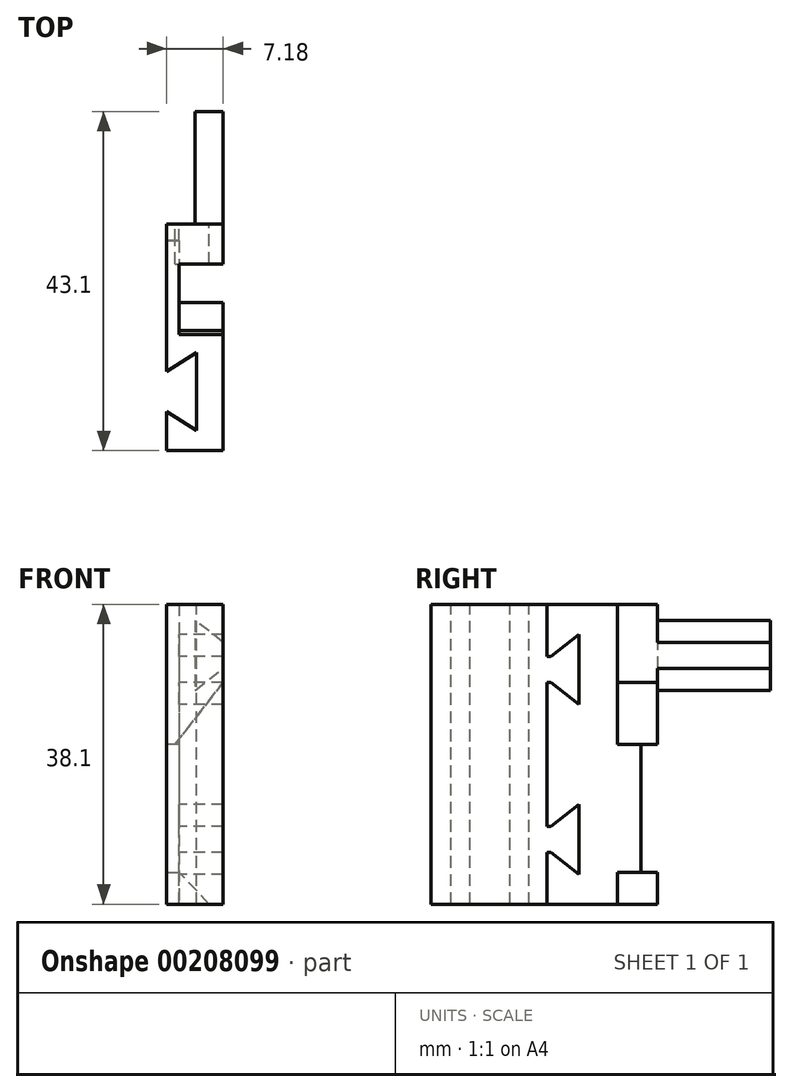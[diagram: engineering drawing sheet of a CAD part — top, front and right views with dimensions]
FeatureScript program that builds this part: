
annotation { "Feature Type Name" : "Feature", "Feature Type Description" : "" }
export const myFeature = defineFeature(function(context is Context, id is Id, definition is map)
    precondition{}
    {
        {
            var Q0;
            Q0=qCreatedBy(makeId("Right.planeOp"),FACE);
            var sketch = newSketch(context, id + "F0", { "sketchPlane" : qUnion([Q0])});
            skLineSegment(sketch, "E0.bottom", {"start": v(-15.24, 38.1) * mm, "end": v(11.43, 38.1) * mm});
            skLineSegment(sketch, "E0.top", {"start": v(-15.24, 0) * mm, "end": v(11.43, 0) * mm});
            skLineSegment(sketch, "E0.right", {"start": v(11.43, 38.1) * mm, "end": v(11.43, 0) * mm});
            skLineSegment(sketch, "E1", {"start": v(-15.24, 38.1) * mm, "end": v(-15.24, 0) * mm});
            skLineSegment(sketch, "E2.bottom", {"start": v(11.43, 38.1) * mm, "end": v(13.54, 38.1) * mm});
            skLineSegment(sketch, "E2.top", {"start": v(11.43, 20.32) * mm, "end": v(13.54, 20.32) * mm});
            skLineSegment(sketch, "E2.left", {"start": v(11.43, 38.1) * mm, "end": v(11.43, 20.32) * mm});
            skLineSegment(sketch, "E2.right", {"start": v(13.54, 38.1) * mm, "end": v(13.54, 20.32) * mm});
            skSolve(sketch);
        }
        {
            var Q0;
            Q0 = qSketchRegion(id + "F0", true);
            extrude(context, id + "F1", {"entities" : qUnion([Q0]), "depth" : 1.59 * mm});
        }
        {
            var Q0;
            Q0=makeQuery(id+"F1.opExtrude","CAP_FACE",FACE,{"disambiguationData":[OSD([sQuery(id+"F0.wireOp",EDGE,"E0.bottom"),sQuery(id+"F0.wireOp",EDGE,"E0.top"),sQuery(id+"F0.wireOp",EDGE,"E0.right"),sQuery(id+"F0.wireOp",EDGE,"E1")])],"isStart":false});
            var sketch = newSketch(context, id + "F2", { "sketchPlane" : qUnion([Q0])});
            skLineSegment(sketch, "E3", {"start": v(0, 31.5) * mm, "end": v(3.56, 34.3) * mm});
            skLineSegment(sketch, "E4", {"start": v(3.56, 34.3) * mm, "end": v(3.56, 25.4) * mm});
            skLineSegment(sketch, "E5", {"start": v(3.56, 25.4) * mm, "end": v(0, 28.2) * mm});
            skLineSegment(sketch, "E6", {"start": v(0, 28.2) * mm, "end": v(0, 31.5) * mm});
            skLineSegment(sketch, "E7", {"start": v(0, 9.9) * mm, "end": v(3.56, 12.7) * mm});
            skLineSegment(sketch, "E8", {"start": v(3.56, 3.8) * mm, "end": v(0, 6.6) * mm});
            skLineSegment(sketch, "E9", {"start": v(0, 6.6) * mm, "end": v(0, 9.9) * mm});
            skLineSegment(sketch, "E10", {"start": v(3.56, 3.8) * mm, "end": v(3.56, 12.7) * mm});
            skSolve(sketch);
        }
        {
            var Q0;
            Q0=makeQuery(id+"F2.imprint","IMPRINT",FACE,{"disambiguationData":[TD([[makeQuery(id+"F2.imprint","IMPRINT",EDGE,{"derivedFrom":sQuery(id+"F2.wireOp",EDGE,"E3")}),-1.0]])]});
            var Q1;
            Q1=makeQuery(id+"F2.imprint","IMPRINT",FACE,{"disambiguationData":[TD([[makeQuery(id+"F2.imprint","IMPRINT",EDGE,{"derivedFrom":sQuery(id+"F2.wireOp",EDGE,"E7")}),-1.0]])]});
            extrude(context, id + "F3", {"entities" : qUnion([Q0, Q1]), "operationType" : NewBodyOperationType.ADD, "depth" : 5.6 * mm});
        }
        {
            var Q0;
            Q0=makeQuery(id+"F1.opExtrude","CAP_FACE",FACE,{"disambiguationData":[OSD([sQuery(id+"F0.wireOp",EDGE,"E0.bottom"),sQuery(id+"F0.wireOp",EDGE,"E0.top"),sQuery(id+"F0.wireOp",EDGE,"E0.right"),sQuery(id+"F0.wireOp",EDGE,"E1")])],"isStart":false});
            var sketch = newSketch(context, id + "F4", { "sketchPlane" : qUnion([Q0])});
            skLineSegment(sketch, "E11.bottom", {"start": v(-15.24, 38.1) * mm, "end": v(-0.5, 38.1) * mm});
            skLineSegment(sketch, "E11.top", {"start": v(-15.24, 0) * mm, "end": v(-0.5, 0) * mm});
            skLineSegment(sketch, "E11.left", {"start": v(-15.24, 38.1) * mm, "end": v(-15.24, 0) * mm});
            skLineSegment(sketch, "E11.right", {"start": v(-0.5, 38.1) * mm, "end": v(-0.5, 0) * mm});
            skSolve(sketch);
        }
        {
            var Q0;
            Q0 = qSketchRegion(id + "F4", true);
            var Q1;
            Q1=makeQuery(id+"F3.opExtrude","CAP_FACE",FACE,{"disambiguationData":[OSD([sQuery(id+"F2.wireOp",EDGE,"E3"),sQuery(id+"F2.wireOp",EDGE,"E4"),sQuery(id+"F2.wireOp",EDGE,"E5"),sQuery(id+"F2.wireOp",EDGE,"E6")])],"isStart":false});
            extrude(context, id + "F5", {"entities" : qUnion([Q0]), "operationType" : NewBodyOperationType.ADD, "endBound" : BoundingType.UP_TO_SURFACE, "endBoundEntityFace" : qUnion([Q1]), "depth" : 25.4 * mm});
        }
        {
            var Q0;
            Q0=makeQuery(id+"F3.opExtrude","SWEPT_FACE",FACE,{"disambiguationData":[OSD([sQuery(id+"F2.wireOp",EDGE,"E6")])]});
            var Q1;
            Q1=makeQuery(id+"F3.opExtrude","SWEPT_FACE",FACE,{"disambiguationData":[OSD([sQuery(id+"F2.wireOp",EDGE,"E9")])]});
            extrude(context, id + "F6", {"entities" : qUnion([Q0, Q1]), "operationType" : NewBodyOperationType.ADD, "depth" : 0.5 * mm});
        }
        {
            var Q0;
            Q0=makeQuery(id+"F5.boolean.opBoolean","MERGE",FACE,{"derivedFrom":[makeQuery(id+"F1.opExtrude","SWEPT_FACE",FACE,{"disambiguationData":[OSD([sQuery(id+"F0.wireOp",EDGE,"E0.bottom"),sQuery(id+"F0.wireOp",EDGE,"E2.bottom")])]}),makeQuery(id+"F5.opExtrude","SWEPT_FACE",FACE,{"disambiguationData":[OSD([sQuery(id+"F4.wireOp",EDGE,"E11.bottom")])]})]});
            var sketch = newSketch(context, id + "F7", { "sketchPlane" : qUnion([Q0])});
            skLineSegment(sketch, "E12", {"start": v(3.81, -2.8) * mm, "end": v(3.81, -12.7) * mm});
            skLineSegment(sketch, "E13", {"start": v(3.81, -12.7) * mm, "end": v(0, -10.29) * mm});
            skLineSegment(sketch, "E14", {"start": v(0, -10.29) * mm, "end": v(0, -5.2) * mm});
            skLineSegment(sketch, "E15", {"start": v(0, -5.2) * mm, "end": v(3.8, -2.8) * mm});
            skSolve(sketch);
        }
        {
            var Q0;
            Q0=makeQuery(id+"F7.imprint","IMPRINT",FACE,{"disambiguationData":[TD([[makeQuery(id+"F7.imprint","IMPRINT",EDGE,{"derivedFrom":sQuery(id+"F7.wireOp",EDGE,"E12")}),-1.0]])]});
            extrude(context, id + "F8", {"entities" : qUnion([Q0]), "operationType" : NewBodyOperationType.REMOVE, "endBound" : BoundingType.THROUGH_ALL, "oppositeDirection" : true, "depth" : 25.4 * mm});
        }
        {
            var Q0;
            Q0=makeQuery(id+"F1.opExtrude","CAP_FACE",FACE,{"disambiguationData":[OSD([sQuery(id+"F0.wireOp",EDGE,"E0.bottom"),sQuery(id+"F0.wireOp",EDGE,"E0.top"),sQuery(id+"F0.wireOp",EDGE,"E0.right"),sQuery(id+"F0.wireOp",EDGE,"E1")])],"isStart":false});
            var sketch = newSketch(context, id + "F9", { "sketchPlane" : qUnion([Q0])});
            skLineSegment(sketch, "E16.bottom", {"start": v(13.54, 38.1) * mm, "end": v(8.46, 38.1) * mm});
            skLineSegment(sketch, "E16.top", {"start": v(13.54, 20.32) * mm, "end": v(8.46, 20.32) * mm});
            skLineSegment(sketch, "E16.left", {"start": v(13.54, 38.1) * mm, "end": v(13.54, 20.32) * mm});
            skLineSegment(sketch, "E16.right", {"start": v(8.46, 38.1) * mm, "end": v(8.46, 20.32) * mm});
            skSolve(sketch);
        }
        {
            var Q0;
            Q0 = qSketchRegion(id + "F9", true);
            var Q1;
            {var subQ0=sQuery(id+"F2.wireOp",EDGE,"E9");var subQ1=sQuery(id+"F2.wireOp",EDGE,"E6");Q1=makeQuery(id+"F6.boolean.opBoolean","MERGE",FACE,{"derivedFrom":[makeQuery(id+"F3.opExtrude","CAP_FACE",FACE,{"disambiguationData":[OSD([sQuery(id+"F2.wireOp",EDGE,"E3"),sQuery(id+"F2.wireOp",EDGE,"E4"),sQuery(id+"F2.wireOp",EDGE,"E5"),subQ1])],"isStart":false}),makeQuery(id+"F3.opExtrude","CAP_FACE",FACE,{"disambiguationData":[OSD([sQuery(id+"F2.wireOp",EDGE,"E7"),sQuery(id+"F2.wireOp",EDGE,"E8"),subQ0,sQuery(id+"F2.wireOp",EDGE,"E10")])],"isStart":false}),makeQuery(id+"F5.opExtrude","CAP_FACE",FACE,{"disambiguationData":[OSD([sQuery(id+"F4.wireOp",EDGE,"E11.bottom"),sQuery(id+"F4.wireOp",EDGE,"E11.top"),sQuery(id+"F4.wireOp",EDGE,"E11.left"),sQuery(id+"F4.wireOp",EDGE,"E11.right")])],"isStart":false}),makeQuery(id+"F6.opExtrude","SWEPT_FACE",FACE,{"disambiguationData":[OSD([subQ1]),TDD([makeQuery(id+"F3.opExtrude","CAP_EDGE",EDGE,{"disambiguationData":[OSD([subQ1])],"isStart":false})])]}),makeQuery(id+"F6.opExtrude","SWEPT_FACE",FACE,{"disambiguationData":[OSD([subQ0]),TDD([makeQuery(id+"F3.opExtrude","CAP_EDGE",EDGE,{"disambiguationData":[OSD([subQ0])],"isStart":false})])]})]});}
            extrude(context, id + "F10", {"entities" : qUnion([Q0]), "operationType" : NewBodyOperationType.ADD, "endBound" : BoundingType.UP_TO_SURFACE, "endBoundEntityFace" : qUnion([Q1]), "depth" : 25.4 * mm});
        }
        {
            var Q0;
            Q0=makeQuery(id+"F10.boolean.opBoolean","MERGE",FACE,{"derivedFrom":[makeQuery(id+"F1.opExtrude","SWEPT_FACE",FACE,{"disambiguationData":[OSD([sQuery(id+"F0.wireOp",EDGE,"E2.right")])]}),makeQuery(id+"F10.opExtrude","SWEPT_FACE",FACE,{"disambiguationData":[OSD([sQuery(id+"F9.wireOp",EDGE,"E16.left")])]})]});
            var sketch = newSketch(context, id + "F11", { "sketchPlane" : qUnion([Q0])});
            skLineSegment(sketch, "E17", {"start": v(-7.18, 20.32) * mm, "end": v(-1.08, 20.32) * mm});
            skLineSegment(sketch, "E18", {"start": v(-1.08, 20.32) * mm, "end": v(-7.18, 28.2) * mm});
            skLineSegment(sketch, "E19", {"start": v(-7.18, 28.2) * mm, "end": v(-7.18, 20.32) * mm});
            skSolve(sketch);
        }
        {
            var Q0;
            Q0 = qSketchRegion(id + "F11", true);
            var Q1;
            Q1=makeQuery(id+"F10.opExtrude","SWEPT_FACE",FACE,{"disambiguationData":[OSD([sQuery(id+"F9.wireOp",EDGE,"E16.right")])]});
            extrude(context, id + "F12", {"entities" : qUnion([Q0]), "operationType" : NewBodyOperationType.REMOVE, "endBound" : BoundingType.UP_TO_SURFACE, "oppositeDirection" : true, "endBoundEntityFace" : qUnion([Q1]), "depth" : 25.4 * mm});
        }
        {
            var Q0;
            Q0=makeQuery(id+"F10.boolean.opBoolean","MERGE",FACE,{"derivedFrom":[makeQuery(id+"F1.opExtrude","SWEPT_FACE",FACE,{"disambiguationData":[OSD([sQuery(id+"F0.wireOp",EDGE,"E2.right")])]}),makeQuery(id+"F10.opExtrude","SWEPT_FACE",FACE,{"disambiguationData":[OSD([sQuery(id+"F9.wireOp",EDGE,"E16.left")])]})]});
            var sketch = newSketch(context, id + "F13", { "sketchPlane" : qUnion([Q0])});
            skLineSegment(sketch, "E20", {"start": v(-7.18, 33.27) * mm, "end": v(-3.62, 36.07) * mm});
            skLineSegment(sketch, "E21", {"start": v(-3.62, 36.07) * mm, "end": v(-3.62, 27.18) * mm});
            skLineSegment(sketch, "E22", {"start": v(-3.62, 27.18) * mm, "end": v(-7.18, 29.97) * mm});
            skLineSegment(sketch, "E23", {"start": v(-7.18, 29.97) * mm, "end": v(-7.18, 33.27) * mm});
            skSolve(sketch);
        }
        {
            var Q0;
            Q0=makeQuery(id+"F13.imprint","IMPRINT",FACE,{"disambiguationData":[TD([[makeQuery(id+"F13.imprint","IMPRINT",EDGE,{"derivedFrom":sQuery(id+"F13.wireOp",EDGE,"E20")}),-1.0]])]});
            extrude(context, id + "F14", {"entities" : qUnion([Q0]), "operationType" : NewBodyOperationType.ADD, "depth" : 14.32 * mm});
        }
        {
            var Q0;
            Q0=makeQuery(id+"F1.opExtrude","CAP_FACE",FACE,{"disambiguationData":[OSD([sQuery(id+"F0.wireOp",EDGE,"E0.bottom"),sQuery(id+"F0.wireOp",EDGE,"E0.top"),sQuery(id+"F0.wireOp",EDGE,"E0.right"),sQuery(id+"F0.wireOp",EDGE,"E1"),sQuery(id+"F0.wireOp",EDGE,"E2.bottom"),sQuery(id+"F0.wireOp",EDGE,"E2.top"),sQuery(id+"F0.wireOp",EDGE,"E2.right")])],"isStart":false});
            var sketch = newSketch(context, id + "F15", { "sketchPlane" : qUnion([Q0])});
            skLineSegment(sketch, "E24.bottom", {"start": v(11.43, 0) * mm, "end": v(8.46, 0) * mm});
            skLineSegment(sketch, "E24.top", {"start": v(11.43, 4.06) * mm, "end": v(8.46, 4.06) * mm});
            skLineSegment(sketch, "E24.left", {"start": v(11.43, 0) * mm, "end": v(11.43, 4.06) * mm});
            skLineSegment(sketch, "E24.right", {"start": v(8.46, 0) * mm, "end": v(8.46, 4.06) * mm});
            skSolve(sketch);
        }
        {
            var Q0;
            Q0 = qSketchRegion(id + "F15", true);
            extrude(context, id + "F16", {"entities" : qUnion([Q0]), "operationType" : NewBodyOperationType.ADD, "depth" : 3.8 * mm});
        }
        {
            var Q0;
            Q0=makeQuery(id+"F16.boolean.opBoolean","MERGE",FACE,{"derivedFrom":[makeQuery(id+"F1.opExtrude","SWEPT_FACE",FACE,{"disambiguationData":[OSD([sQuery(id+"F0.wireOp",EDGE,"E0.right")])]}),makeQuery(id+"F16.opExtrude","SWEPT_FACE",FACE,{"disambiguationData":[OSD([sQuery(id+"F15.wireOp",EDGE,"E24.left")])]})]});
            var sketch = newSketch(context, id + "F17", { "sketchPlane" : qUnion([Q0])});
            skLineSegment(sketch, "E25.bottom", {"start": v(0, 0) * mm, "end": v(-5.4, 0) * mm});
            skLineSegment(sketch, "E25.top", {"start": v(0, 4.06) * mm, "end": v(-5.4, 4.06) * mm});
            skLineSegment(sketch, "E25.left", {"start": v(0, 0) * mm, "end": v(0, 4.06) * mm});
            skLineSegment(sketch, "E25.right", {"start": v(-5.4, 0) * mm, "end": v(-5.4, 4.06) * mm});
            skSolve(sketch);
        }
        {
            var Q0;
            Q0 = qSketchRegion(id + "F17", true);
            var Q1;
            Q1=makeQuery(id+"F10.boolean.opBoolean","MERGE",FACE,{"derivedFrom":[makeQuery(id+"F1.opExtrude","SWEPT_FACE",FACE,{"disambiguationData":[OSD([sQuery(id+"F0.wireOp",EDGE,"E2.right")])]}),makeQuery(id+"F10.opExtrude","SWEPT_FACE",FACE,{"disambiguationData":[OSD([sQuery(id+"F9.wireOp",EDGE,"E16.left")])]})]});
            extrude(context, id + "F18", {"entities" : qUnion([Q0]), "operationType" : NewBodyOperationType.ADD, "endBound" : BoundingType.UP_TO_SURFACE, "endBoundEntityFace" : qUnion([Q1]), "depth" : 25.4 * mm});
        }
        {
            var Q0;
            Q0=makeQuery(id+"F18.opExtrude","CAP_FACE",FACE,{"disambiguationData":[OSD([sQuery(id+"F17.wireOp",EDGE,"E25.bottom"),sQuery(id+"F17.wireOp",EDGE,"E25.top"),sQuery(id+"F17.wireOp",EDGE,"E25.left"),sQuery(id+"F17.wireOp",EDGE,"E25.right")])],"isStart":false});
            var sketch = newSketch(context, id + "F19", { "sketchPlane" : qUnion([Q0])});
            skLineSegment(sketch, "E26", {"start": v(-5.4, 4.06) * mm, "end": v(-5.4, 0) * mm});
            skLineSegment(sketch, "E27", {"start": v(-5.4, 0) * mm, "end": v(-1.59, 4.06) * mm});
            skLineSegment(sketch, "E28", {"start": v(-1.59, 4.06) * mm, "end": v(-5.4, 4.06) * mm});
            skSolve(sketch);
        }
        {
            var Q0;
            Q0 = qSketchRegion(id + "F19", true);
            var Q1;
            Q1=makeQuery(id+"F16.opExtrude","SWEPT_FACE",FACE,{"disambiguationData":[OSD([sQuery(id+"F15.wireOp",EDGE,"E24.right")])]});
            extrude(context, id + "F20", {"entities" : qUnion([Q0]), "operationType" : NewBodyOperationType.REMOVE, "endBound" : BoundingType.UP_TO_SURFACE, "oppositeDirection" : true, "endBoundEntityFace" : qUnion([Q1]), "depth" : 25.4 * mm});
        }
    });
